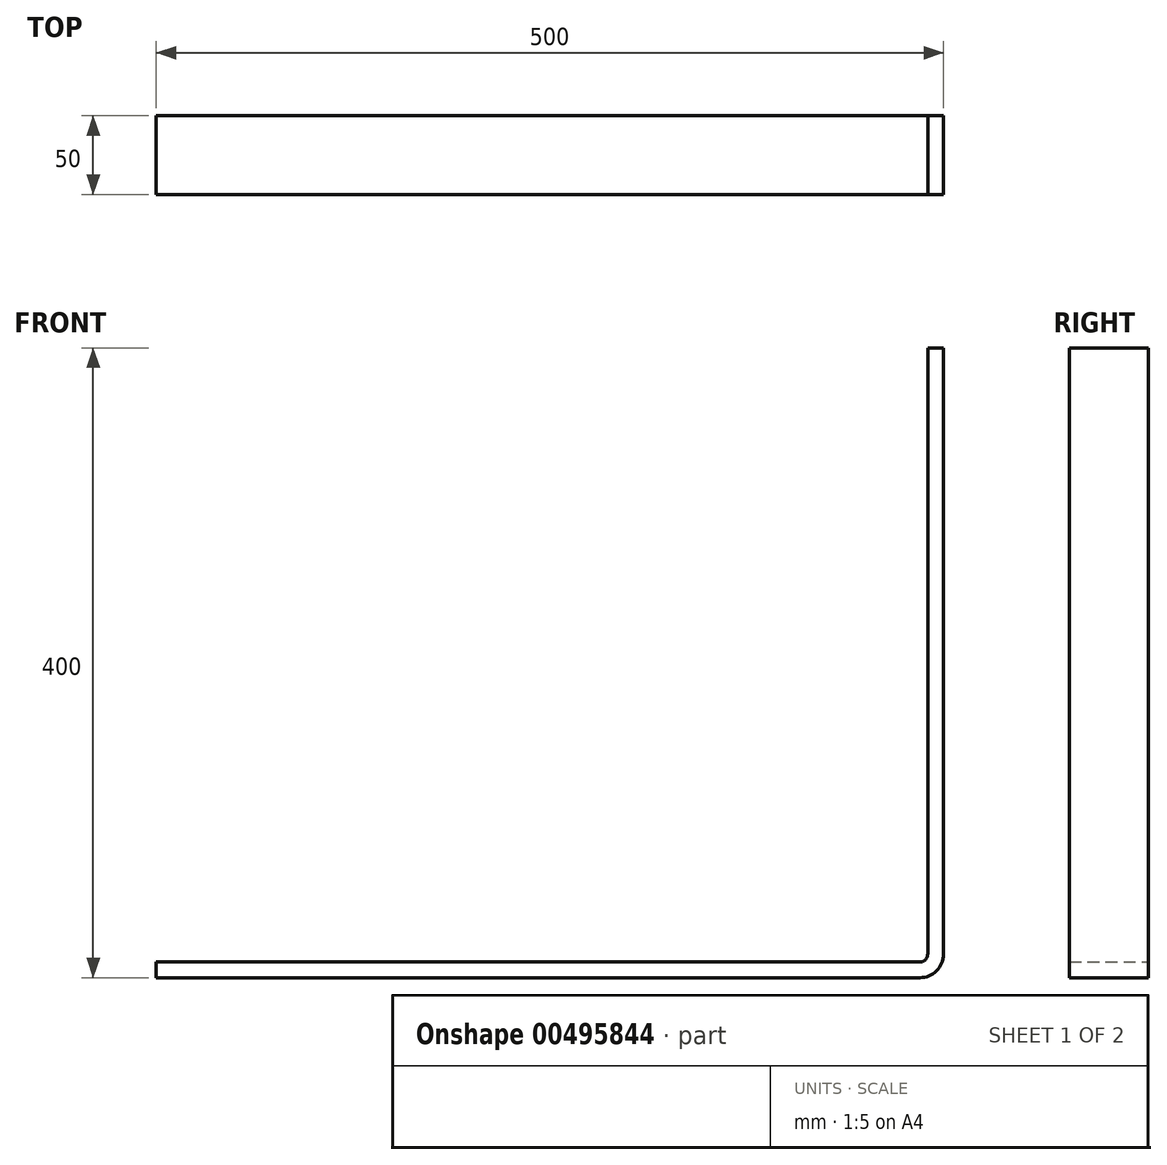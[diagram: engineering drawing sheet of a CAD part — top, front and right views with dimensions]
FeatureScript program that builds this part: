
annotation { "Feature Type Name" : "Feature", "Feature Type Description" : "" }
export const myFeature = defineFeature(function(context is Context, id is Id, definition is map)
    precondition{}
    {
        {
            var Q0;
            Q0=qCreatedBy(makeId("Front.planeOp"),FACE);
            var sketch = newSketch(context, id + "F0", { "sketchPlane" : qUnion([Q0])});
            skLineSegment(sketch, "E0", {"start": v(-475.17, 0) * mm, "end": v(-475.17, 10) * mm});
            skLineSegment(sketch, "E1", {"start": v(-475.17, 10) * mm, "end": v(9.83, 10) * mm});
            skLineSegment(sketch, "E2", {"start": v(14.83, 15) * mm, "end": v(14.83, 400) * mm});
            skLineSegment(sketch, "E3", {"start": v(14.83, 400) * mm, "end": v(24.83, 400) * mm});
            skLineSegment(sketch, "E4", {"start": v(24.83, 400) * mm, "end": v(24.83, 15) * mm});
            skLineSegment(sketch, "E5", {"start": v(9.83, 0) * mm, "end": v(-475.17, 0) * mm});
            skPoint(sketch, "E6.visualSharp", {"position": v(24.83, 0) * mm});
            skArc(sketch, "E6.filletArc", {"start": v(9.83, 0) * mm, "mid": v(20.43, 4.4) * mm, "end": v(24.83, 15) * mm});
            skPoint(sketch, "E7.visualSharp", {"position": v(14.83, 10) * mm});
            skArc(sketch, "E7.filletArc", {"start": v(9.83, 10) * mm, "mid": v(13.36, 11.46) * mm, "end": v(14.83, 15) * mm});
            skSolve(sketch);
        }
        {
            var Q0;
            Q0=qSketchRegion(id+"F0",true);
            extrude(context, id + "F1", {"entities" : qUnion([Q0]), "depth" : 50 * mm});
        }
    });
